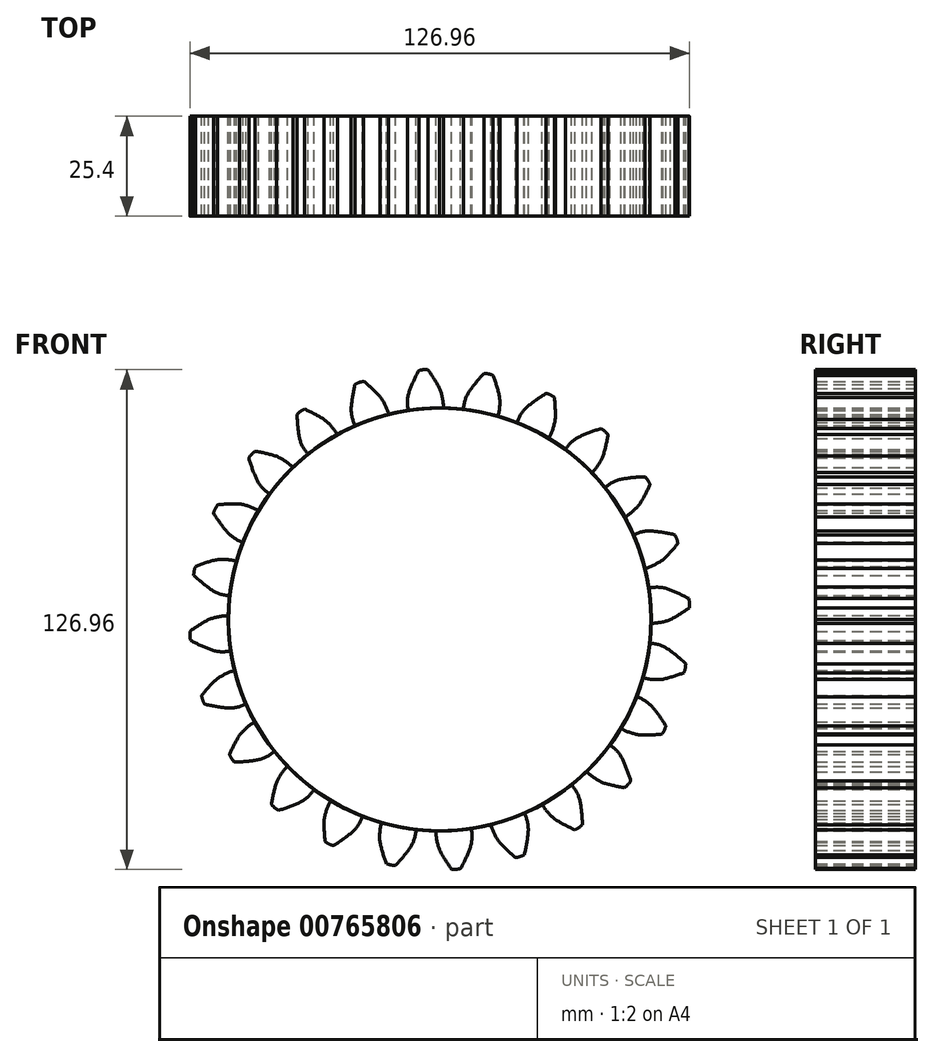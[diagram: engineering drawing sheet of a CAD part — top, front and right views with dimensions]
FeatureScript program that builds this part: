
annotation { "Feature Type Name" : "Feature", "Feature Type Description" : "" }
export const myFeature = defineFeature(function(context is Context, id is Id, definition is map)
    precondition{}
    {
        {
            var Q0;
            Q0=qCreatedBy(makeId("Front.planeOp"),FACE);
            var sketch = newSketch(context, id + "F0", { "sketchPlane" : qUnion([Q0])});
            skCircle(sketch, "E0", {"center": v(0, 0) * mm, "radius": 63.5 * mm, "construction": true});
            skCircle(sketch, "E1", {"center": v(0, 0) * mm, "radius": 58.67 * mm, "construction": true});
            skCircle(sketch, "E2", {"center": v(0, 0) * mm, "radius": 53.72 * mm});
            skLineSegment(sketch, "E3", {"start": v(0, 0) * mm, "end": v(0, 126.12) * mm, "construction": true});
            skLineSegment(sketch, "E4", {"start": v(0, 0) * mm, "end": v(-8.4, 128.12) * mm, "construction": true});
            skLineSegment(sketch, "E5", {"start": v(0, 58.67) * mm, "end": v(-101.93, 58.67) * mm, "construction": true});
            skLineSegment(sketch, "E6", {"start": v(0, 58.67) * mm, "end": v(-103.98, 20.83) * mm, "construction": true});
            skCircle(sketch, "E7", {"center": v(0, 0) * mm, "radius": 55.14 * mm, "construction": true});
            skCircle(sketch, "E8", {"center": v(0, 58.67) * mm, "radius": 14.6 * mm, "construction": true});
            skCircle(sketch, "E9", {"center": v(-13.63, 53.42) * mm, "radius": 14.6 * mm});
            skArc(sketch, "E10", {"start": v(0, 58.67) * mm, "mid": v(-1.4, 61.1) * mm, "end": v(-2.99, 63.43) * mm});
            skArc(sketch, "E11", {"start": v(0.97, 53.71) * mm, "mid": v(0.85, 56.27) * mm, "end": v(0, 58.67) * mm});
            skArc(sketch, "E12.MirrorCS", {"start": v(-7.66, 58.17) * mm, "mid": v(-6.58, 60.77) * mm, "end": v(-5.32, 63.28) * mm});
            skArc(sketch, "E13.MirrorCS", {"start": v(-7.98, 53.13) * mm, "mid": v(-8.2, 55.67) * mm, "end": v(-7.66, 58.17) * mm});
            skArc(sketch, "E14", {"start": v(-2.99, 63.43) * mm, "mid": v(-4.16, 63.47) * mm, "end": v(-5.32, 63.28) * mm});
            skSolve(sketch);
        }
        {
            var Q0;
            {var subQ0=sQuery(id+"F0.wireOp",EDGE,"E9");var subQ1=sQuery(id+"F0.wireOp",EDGE,"E2");var subQ3=makeQuery(id+"F0.imprint","INTERSECT",VERTEX,{"derivedFrom":[subQ1,subQ0]});Q0=makeQuery(id+"F0.imprint","IMPRINT",FACE,{"disambiguationData":[TD([[makeQuery(id+"F0.imprint","IMPRINT",EDGE,{"disambiguationData":[TD([[subQ3,-1.0]])],"derivedFrom":subQ1}),1.0]])]});}
            var Q1;
            {var subQ1=sQuery(id+"F0.wireOp",EDGE,"E2");var subQ3=makeQuery(id+"F0.imprint","INTERSECT",VERTEX,{"derivedFrom":[subQ1,sQuery(id+"F0.wireOp",EDGE,"E13.MirrorCS")]});Q1=makeQuery(id+"F0.imprint","IMPRINT",FACE,{"disambiguationData":[TD([[makeQuery(id+"F0.imprint","IMPRINT",EDGE,{"disambiguationData":[TD([[subQ3,-1.0]])],"derivedFrom":subQ1}),1.0]])]});}
            var Q2;
            {var subQ0=sQuery(id+"F0.wireOp",EDGE,"E10");Q2=makeQuery(id+"F0.imprint","IMPRINT",FACE,{"disambiguationData":[TD([[makeQuery(id+"F0.imprint","IMPRINT",EDGE,{"derivedFrom":subQ0}),1.0]])]});}
            extrude(context, id + "F1", {"entities" : qUnion([Q0, Q1, Q2]), "depth" : 25.4 * mm, "offsetDistance" : 25.4 * mm});
        }
        {
            var Q0;
            Q0=makeQuery(id+"F1.opExtrude","SWEPT_BODY",BODY,{"disambiguationData":[OSD([sQuery(id+"F0.wireOp",EDGE,"E2"),sQuery(id+"F0.wireOp",EDGE,"E9"),sQuery(id+"F0.wireOp",EDGE,"E10"),sQuery(id+"F0.wireOp",EDGE,"E12.MirrorCS"),sQuery(id+"F0.wireOp",EDGE,"E13.MirrorCS"),sQuery(id+"F0.wireOp",EDGE,"E14")])]});
            var Q1;
            Q1=makeQuery(id+"F1.opExtrude","SWEPT_FACE",FACE,{"disambiguationData":[OSD([sQuery(id+"F0.wireOp",EDGE,"E2")])]});
            circularPattern(context, id + "F2", {"entities" : qUnion([Q0]), "axis" : qUnion([Q1]), "angle" : 360 * degree, "instanceCount" : 24, "equalSpace" : true});
        }
    });
